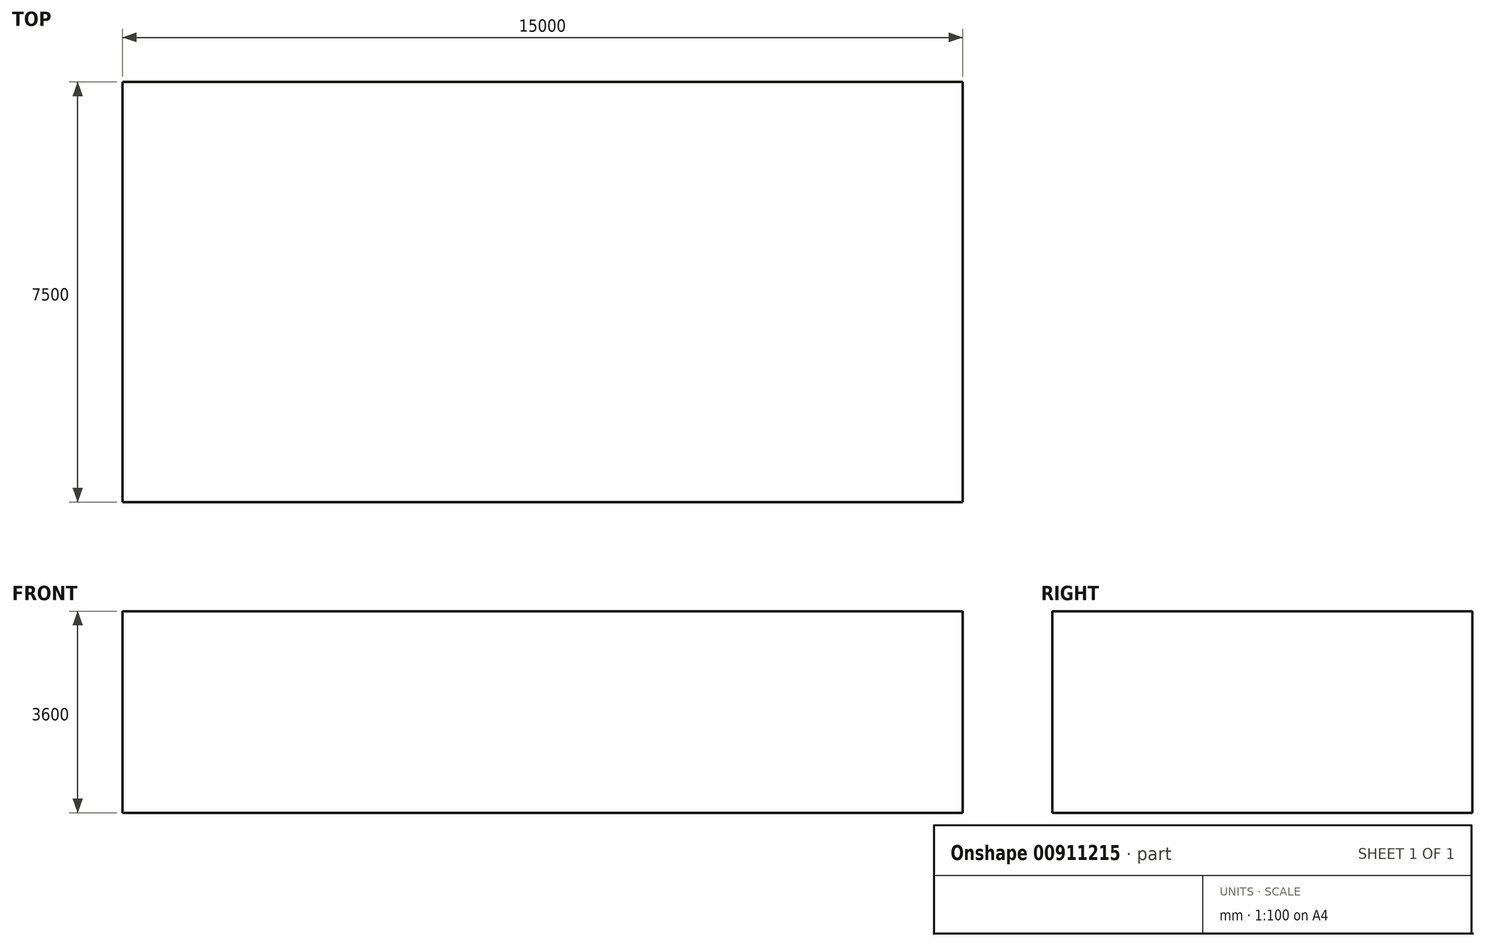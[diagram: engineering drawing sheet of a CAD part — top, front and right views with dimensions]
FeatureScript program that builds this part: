
annotation { "Feature Type Name" : "Feature", "Feature Type Description" : "" }
export const myFeature = defineFeature(function(context is Context, id is Id, definition is map)
    precondition{}
    {
        {
            var Q0;
            Q0=qCreatedBy(makeId("Top.planeOp"),FACE);
            var sketch = newSketch(context, id + "F0", { "sketchPlane" : qUnion([Q0])});
            skLineSegment(sketch, "E0.bottom", {"start": v(-7500, 3750) * mm, "end": v(7500, 3750) * mm});
            skLineSegment(sketch, "E0.top", {"start": v(-7500, -3750) * mm, "end": v(7500, -3750) * mm});
            skLineSegment(sketch, "E0.left", {"start": v(-7500, 3750) * mm, "end": v(-7500, -3750) * mm});
            skLineSegment(sketch, "E0.right", {"start": v(7500, 3750) * mm, "end": v(7500, -3750) * mm});
            skPoint(sketch, "E0.middle", {"position": v(0, 0) * mm});
            skSolve(sketch);
        }
        {
            var Q0;
            Q0 = qSketchRegion(id + "F0", true);
            extrude(context, id + "F1", {"entities" : qUnion([Q0]), "depth" : 3600 * mm, "offsetDistance" : 25 * mm});
        }
    });
